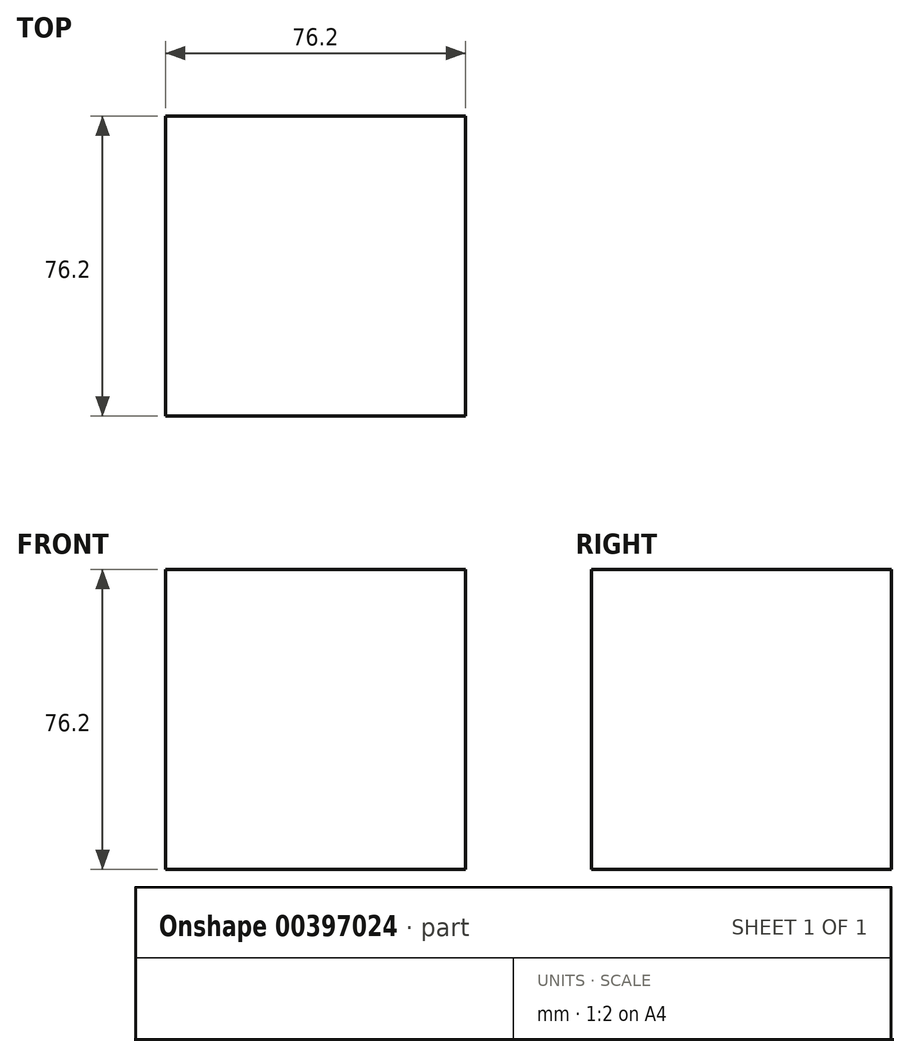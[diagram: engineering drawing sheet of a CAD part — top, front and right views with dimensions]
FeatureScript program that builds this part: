
annotation { "Feature Type Name" : "Feature", "Feature Type Description" : "" }
export const myFeature = defineFeature(function(context is Context, id is Id, definition is map)
    precondition{}
    {
        {
            var Q0;
            Q0=qCreatedBy(makeId("Front.planeOp"),FACE);
            var sketch = newSketch(context, id + "F0", { "sketchPlane" : qUnion([Q0])});
            skLineSegment(sketch, "E0.bottom", {"start": v(-46.45, 55.72) * mm, "end": v(29.75, 55.72) * mm});
            skLineSegment(sketch, "E0.top", {"start": v(-46.45, -20.48) * mm, "end": v(29.75, -20.48) * mm});
            skLineSegment(sketch, "E0.left", {"start": v(-46.45, 55.72) * mm, "end": v(-46.45, -20.48) * mm});
            skLineSegment(sketch, "E0.right", {"start": v(29.75, 55.72) * mm, "end": v(29.75, -20.48) * mm});
            skSolve(sketch);
        }
        {
            var Q0;
            Q0 = qSketchRegion(id + "F0", true);
            extrude(context, id + "F1", {"entities" : qUnion([Q0]), "depth" : 76.2 * mm});
        }
    });
